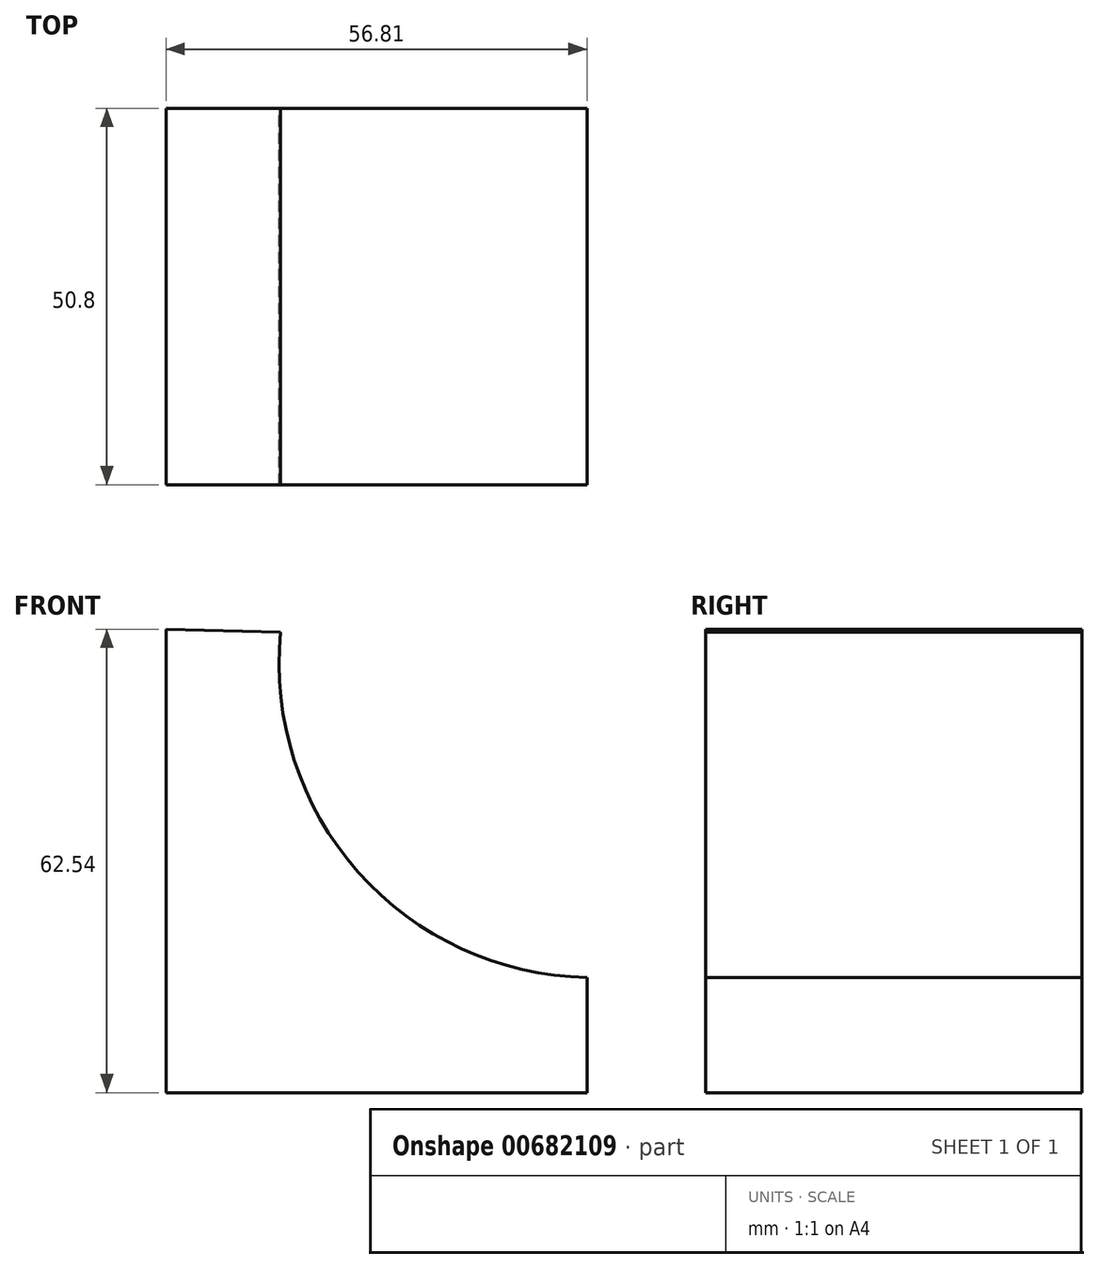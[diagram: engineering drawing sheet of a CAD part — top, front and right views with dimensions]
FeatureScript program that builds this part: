
annotation { "Feature Type Name" : "Feature", "Feature Type Description" : "" }
export const myFeature = defineFeature(function(context is Context, id is Id, definition is map)
    precondition{}
    {
        {
            var Q0;
            Q0=qCreatedBy(makeId("Front.planeOp"),FACE);
            var sketch = newSketch(context, id + "F0", { "sketchPlane" : qUnion([Q0])});
            skLineSegment(sketch, "E0", {"start": v(-56.8, 62.54) * mm, "end": v(-56.8, 0) * mm});
            skLineSegment(sketch, "E1", {"start": v(-56.8, 0) * mm, "end": v(0, 0) * mm});
            skLineSegment(sketch, "E2", {"start": v(0, 0) * mm, "end": v(0, 15.56) * mm});
            skArc(sketch, "E3", {"start": v(-41.34, 62.16) * mm, "mid": v(-30.9, 29.78) * mm, "end": v(0, 15.56) * mm});
            skLineSegment(sketch, "E4", {"start": v(-56.8, 62.54) * mm, "end": v(-41.34, 62.16) * mm});
            skSolve(sketch);
        }
        {
            var Q0;
            Q0 = qSketchRegion(id + "F0", true);
            extrude(context, id + "F1", {"entities" : qUnion([Q0]), "depth" : 50.8 * mm, "offsetDistance" : 25.4 * mm});
        }
    });
